# Revit family: AD-S802T Loudspeaker Face-Based
name_source: partatom
category: Generic Models
revit_build: Autodesk Revit 2015 (Build: 20150511_0715(x64)
units: mm (PartAtom-declared; Revit-internal decimal feet)

## types (3) — shared parameters
Coverage Horizontal = 150
Coverage Vertical = 15
Current Draw = 120
Default Elevation = 4' - 0"
Depth = 5.0in(126mm)
Description = Column Surface-Mount Loudspeaker
Height = 23.4in(595mm)
Impedance = 8
Manufacturer = QSC
Manufacturer URL = https://www.qsc.com
Model = AD-S802T
Power Handling = 120
Product Documentation Link = https://www.qsc.com
Product Page URL = https://www.qsc.com
SPL Max = 116
Sensitivity = 89
Weight = 13.7lb(6.2kg)
Width = 5.2in(131mm)

## per-type parameters (varying)
| type | Mount Position |
| Mount Position 1 | AD-S802T Loudspeaker : Mount Position 1 |
| Mount Position 2 | AD-S802T Loudspeaker : Mount Position 2 |
| Mount Position 3 | AD-S802T Loudspeaker : Mount Position 3 |

## geometry (parser evidence)
native form markers: Blend x4, Sweep x9
no freeform markers — native parametric forms only
